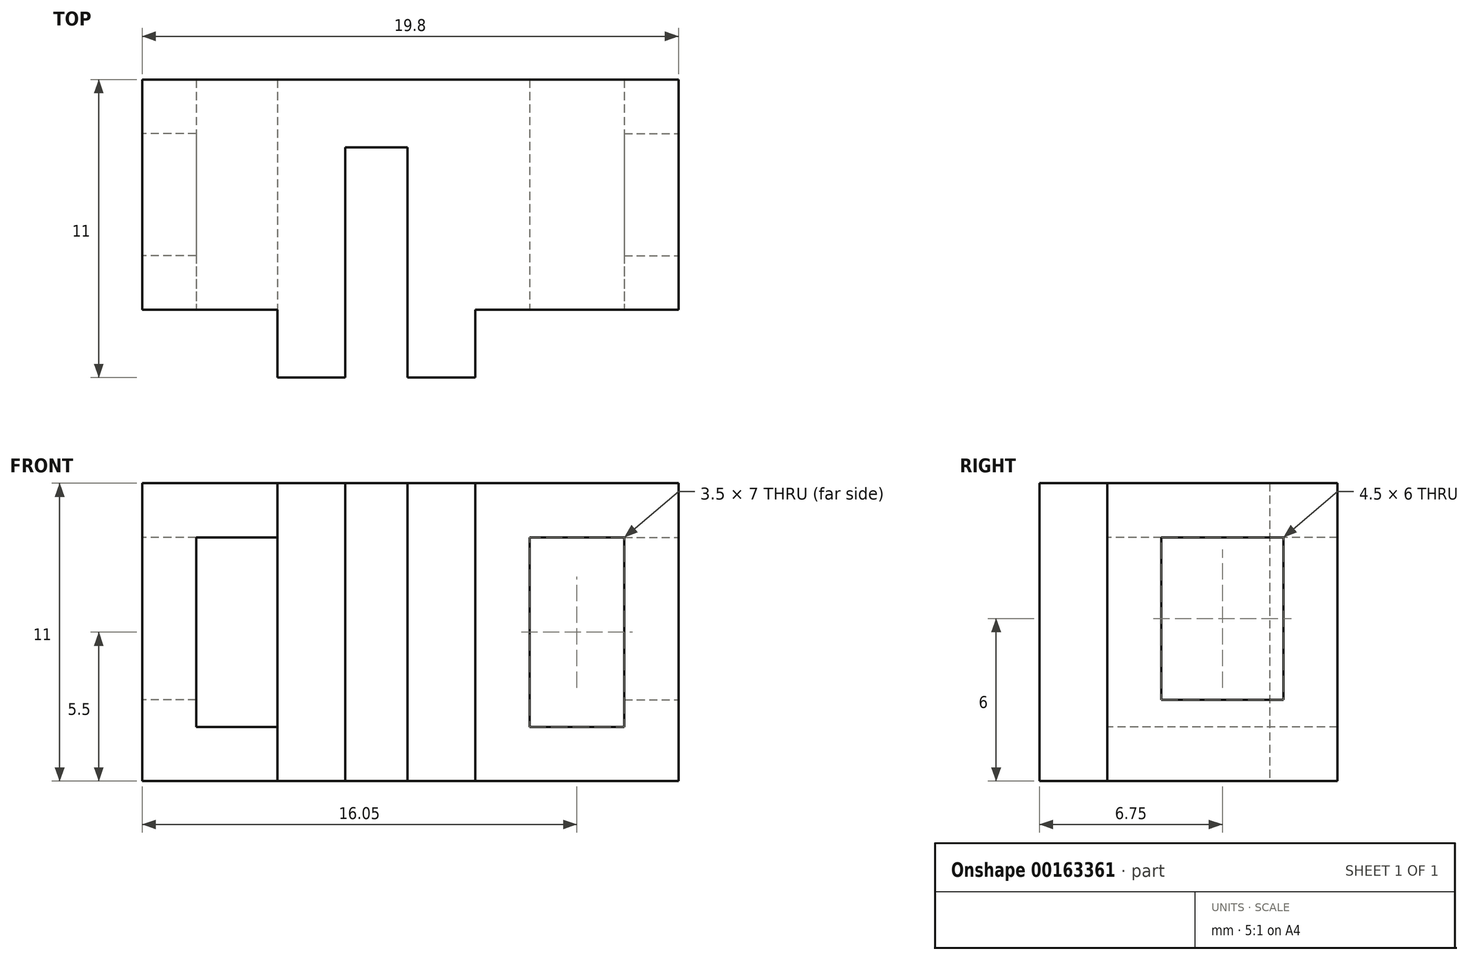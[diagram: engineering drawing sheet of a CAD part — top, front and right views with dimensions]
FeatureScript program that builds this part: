
annotation { "Feature Type Name" : "Feature", "Feature Type Description" : "" }
export const myFeature = defineFeature(function(context is Context, id is Id, definition is map)
    precondition{}
    {
        {
            var Q0;
            Q0=qCreatedBy(makeId("Top.planeOp"),FACE);
            var sketch = newSketch(context, id + "F0", { "sketchPlane" : qUnion([Q0])});
            skLineSegment(sketch, "E0", {"start": v(0, 0) * mm, "end": v(0, -8.5) * mm});
            skLineSegment(sketch, "E1", {"start": v(0, -8.5) * mm, "end": v(-7.5, -8.5) * mm});
            skLineSegment(sketch, "E2", {"start": v(-10, -2.5) * mm, "end": v(-12.3, -2.5) * mm});
            skLineSegment(sketch, "E3", {"start": v(-14.8, -8.5) * mm, "end": v(-19.8, -8.5) * mm});
            skLineSegment(sketch, "E4", {"start": v(-19.8, -8.5) * mm, "end": v(-19.8, 0) * mm});
            skLineSegment(sketch, "E5", {"start": v(-19.8, 0) * mm, "end": v(0, 0) * mm});
            skLineSegment(sketch, "E6", {"start": v(-7.5, -8.5) * mm, "end": v(-7.5, -11) * mm});
            skLineSegment(sketch, "E7", {"start": v(-7.5, -11) * mm, "end": v(-10, -11) * mm});
            skLineSegment(sketch, "E8", {"start": v(-10, -11) * mm, "end": v(-10, -2.5) * mm});
            skLineSegment(sketch, "E9", {"start": v(-12.3, -2.5) * mm, "end": v(-12.3, -11) * mm});
            skLineSegment(sketch, "E10", {"start": v(-12.3, -11) * mm, "end": v(-14.8, -11) * mm});
            skLineSegment(sketch, "E11", {"start": v(-14.8, -11) * mm, "end": v(-14.8, -8.5) * mm});
            skLineSegment(sketch, "E12", {"start": v(-11.15, -2.5) * mm, "end": v(-11.15, 0) * mm, "construction": true});
            skSolve(sketch);
        }
        {
            var Q0;
            Q0=qSketchRegion(id+"F0",true);
            extrude(context, id + "F1", {"entities" : qUnion([Q0]), "depth" : 11 * mm});
        }
        {
            var Q0;
            Q0=makeQuery(id+"F1.opExtrude","SWEPT_FACE",FACE,{"disambiguationData":[OSD([sQuery(id+"F0.wireOp",EDGE,"E4")])]});
            var sketch = newSketch(context, id + "F2", { "sketchPlane" : qUnion([Q0])});
            skLineSegment(sketch, "E13.bottom", {"start": v(6.5, 3) * mm, "end": v(2, 3) * mm});
            skLineSegment(sketch, "E13.top", {"start": v(6.5, 9) * mm, "end": v(2, 9) * mm});
            skLineSegment(sketch, "E13.left", {"start": v(6.5, 3) * mm, "end": v(6.5, 9) * mm});
            skLineSegment(sketch, "E13.right", {"start": v(2, 3) * mm, "end": v(2, 9) * mm});
            skSolve(sketch);
        }
        {
            var Q0;
            Q0=qSketchRegion(id+"F2",true);
            var Q1;
            Q1=makeQuery(id+"F1.opExtrude","SWEPT_FACE",FACE,{"disambiguationData":[OSD([sQuery(id+"F0.wireOp",EDGE,"E11")])]});
            extrude(context, id + "F3", {"entities" : qUnion([Q0]), "operationType" : NewBodyOperationType.REMOVE, "endBound" : BoundingType.UP_TO_SURFACE, "oppositeDirection" : true, "endBoundEntityFace" : qUnion([Q1]), "depth" : 25 * mm});
        }
        {
            var Q0;
            Q0=makeQuery(id+"F1.opExtrude","SWEPT_FACE",FACE,{"disambiguationData":[OSD([sQuery(id+"F0.wireOp",EDGE,"E3")])]});
            var sketch = newSketch(context, id + "F4", { "sketchPlane" : qUnion([Q0])});
            skLineSegment(sketch, "E14.0", {"start": v(-14.8, 11) * mm, "end": v(-14.8, 0) * mm});
            skLineSegment(sketch, "E15", {"start": v(-14.8, 9) * mm, "end": v(-17.8, 9) * mm});
            skLineSegment(sketch, "E16", {"start": v(-17.8, 9) * mm, "end": v(-17.8, 2) * mm});
            skLineSegment(sketch, "E17", {"start": v(-17.8, 2) * mm, "end": v(-14.8, 2) * mm});
            skLineSegment(sketch, "E18.0", {"start": v(-19.8, 11) * mm, "end": v(-19.8, 0) * mm, "construction": true});
            skLineSegment(sketch, "E18.1", {"start": v(-14.8, 11) * mm, "end": v(-19.8, 11) * mm, "construction": true});
            skLineSegment(sketch, "E18.2", {"start": v(-14.8, 0) * mm, "end": v(-19.8, 0) * mm, "construction": true});
            skLineSegment(sketch, "E19", {"start": v(-19.8, 5.5) * mm, "end": v(-17.8, 5.5) * mm, "construction": true});
            skLineSegment(sketch, "E20", {"start": v(-17.3, 11) * mm, "end": v(-17.3, 9) * mm, "construction": true});
            skLineSegment(sketch, "E21", {"start": v(-17.3, 0) * mm, "end": v(-17.3, 2) * mm, "construction": true});
            skSolve(sketch);
        }
        {
            var Q0;
            Q0=qSketchRegion(id+"F4",true);
            extrude(context, id + "F5", {"entities" : qUnion([Q0]), "operationType" : NewBodyOperationType.REMOVE, "endBound" : BoundingType.THROUGH_ALL, "oppositeDirection" : true, "depth" : 25 * mm});
        }
        {
            var Q0;
            Q0=makeQuery(id+"FExIFfINUFs5d3k_1.boolean.opBoolean","MERGE",FACE,{"derivedFrom":[makeQuery(id+"F1.opExtrude","SWEPT_FACE",FACE,{"disambiguationData":[OSD([sQuery(id+"F0.wireOp",EDGE,"E0")])]}),makeQuery(id+"FExIFfINUFs5d3k_1.opExtrude","SWEPT_FACE",FACE,{"disambiguationData":[OSD([sQuery(id+"FvLwcGfzb3WHsGL_1.wireOp",EDGE,"0Dh4MtOT-QXCp-xnXO-UDwR-wMWLb3uXQ4tA.left")])]})]});
            var sketch = newSketch(context, id + "F6", { "sketchPlane" : qUnion([Q0])});
            skLineSegment(sketch, "E22.bottom", {"start": v(-2, 3) * mm, "end": v(-6.5, 3) * mm});
            skLineSegment(sketch, "E22.top", {"start": v(-2, 9) * mm, "end": v(-6.5, 9) * mm});
            skLineSegment(sketch, "E22.left", {"start": v(-2, 3) * mm, "end": v(-2, 9) * mm});
            skLineSegment(sketch, "E22.right", {"start": v(-6.5, 3) * mm, "end": v(-6.5, 9) * mm});
            skSolve(sketch);
        }
        {
            var Q0;
            Q0=qSketchRegion(id+"F6",true);
            extrude(context, id + "F7", {"entities" : qUnion([Q0]), "operationType" : NewBodyOperationType.REMOVE, "oppositeDirection" : true, "depth" : 5 * mm});
        }
        {
            var Q0;
            Q0=makeQuery(id+"FExIFfINUFs5d3k_1.boolean.opBoolean","MERGE",FACE,{"derivedFrom":[makeQuery(id+"F1.opExtrude","SWEPT_FACE",FACE,{"disambiguationData":[OSD([sQuery(id+"F0.wireOp",EDGE,"E1")])]}),makeQuery(id+"FExIFfINUFs5d3k_1.opExtrude","SWEPT_FACE",FACE,{"disambiguationData":[OSD([sQuery(id+"FvLwcGfzb3WHsGL_1.wireOp",EDGE,"0Dh4MtOT-QXCp-xnXO-UDwR-wMWLb3uXQ4tA.bottom")])]})]});
            var sketch = newSketch(context, id + "F8", { "sketchPlane" : qUnion([Q0])});
            skLineSegment(sketch, "E23", {"start": v(-7.5, 11) * mm, "end": v(0, 11) * mm, "construction": true});
            skLineSegment(sketch, "E24", {"start": v(0, 11) * mm, "end": v(0, 0) * mm, "construction": true});
            skLineSegment(sketch, "E25", {"start": v(0, 0) * mm, "end": v(-7.5, 0) * mm, "construction": true});
            skLineSegment(sketch, "E26", {"start": v(-7.5, 0) * mm, "end": v(-7.5, 11) * mm, "construction": true});
            skLineSegment(sketch, "E27.0", {"start": v(-2, 9) * mm, "end": v(-2, 2) * mm});
            skLineSegment(sketch, "E27.1", {"start": v(-5.5, 9) * mm, "end": v(-2, 9) * mm});
            skLineSegment(sketch, "E27.2", {"start": v(-5.5, 2) * mm, "end": v(-5.5, 9) * mm});
            skLineSegment(sketch, "E27.3", {"start": v(-2, 2) * mm, "end": v(-5.5, 2) * mm});
            skSolve(sketch);
        }
        {
            var Q0;
            Q0=qSketchRegion(id+"F8",true);
            extrude(context, id + "F9", {"entities" : qUnion([Q0]), "operationType" : NewBodyOperationType.REMOVE, "endBound" : BoundingType.THROUGH_ALL, "oppositeDirection" : true, "depth" : 25 * mm});
        }
    });
